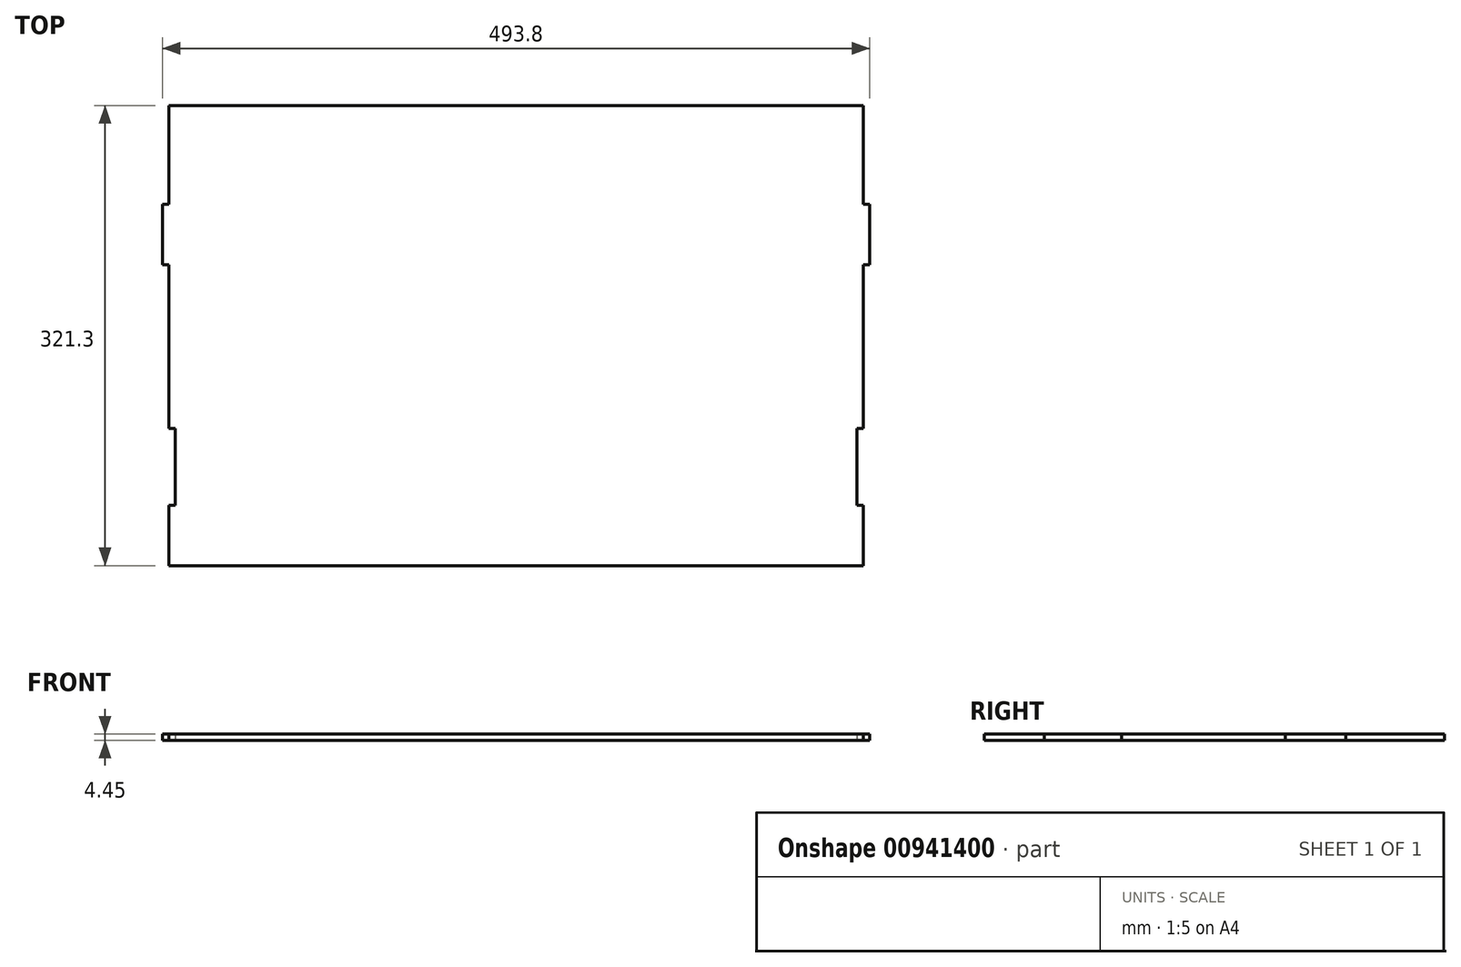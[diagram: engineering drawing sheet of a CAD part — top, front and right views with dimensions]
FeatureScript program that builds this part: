
annotation { "Feature Type Name" : "Feature", "Feature Type Description" : "" }
export const myFeature = defineFeature(function(context is Context, id is Id, definition is map)
    precondition{}
    {
        {
            var Q0;
            Q0=qCreatedBy(makeId("Top.planeOp"),FACE);
            var sketch = newSketch(context, id + "F0", { "sketchPlane" : qUnion([Q0])});
            skLineSegment(sketch, "E0.bottom", {"start": v(238, -73.7) * mm, "end": v(-238, -73.7) * mm});
            skLineSegment(sketch, "E0.left", {"start": v(238, -31.63) * mm, "end": v(238, 22.07) * mm});
            skLineSegment(sketch, "E1.bottom", {"start": v(238, 75.7) * mm, "end": v(242.45, 75.7) * mm});
            skLineSegment(sketch, "E1.top", {"start": v(238, 22.07) * mm, "end": v(242.45, 22.07) * mm});
            skLineSegment(sketch, "E1.right", {"start": v(242.45, 75.7) * mm, "end": v(242.45, 22.07) * mm});
            skLineSegment(sketch, "E2.bottom", {"start": v(238, -73.7) * mm, "end": v(242.45, -73.7) * mm});
            skLineSegment(sketch, "E2.top", {"start": v(238, -31.63) * mm, "end": v(242.45, -31.63) * mm});
            skLineSegment(sketch, "E2.right", {"start": v(242.45, -73.7) * mm, "end": v(242.45, -31.63) * mm});
            skLineSegment(sketch, "E3.left", {"start": v(238, 22.07) * mm, "end": v(238, -28.25) * mm});
            skLineSegment(sketch, "E4.MirrorCS", {"start": v(-242.45, -73.7) * mm, "end": v(-242.45, -31.63) * mm});
            skLineSegment(sketch, "E5.MirrorCS", {"start": v(-242.45, 75.7) * mm, "end": v(-242.45, 22.07) * mm});
            skLineSegment(sketch, "E6.MirrorCS", {"start": v(-238, 22.07) * mm, "end": v(-242.45, 22.07) * mm});
            skLineSegment(sketch, "E7.MirrorCS", {"start": v(-238, -31.63) * mm, "end": v(-238, 22.07) * mm});
            skLineSegment(sketch, "E8.MirrorCS", {"start": v(-238, -31.63) * mm, "end": v(-242.45, -31.63) * mm});
            skLineSegment(sketch, "E9.MirrorCS", {"start": v(-238, -73.7) * mm, "end": v(-242.45, -73.7) * mm});
            skLineSegment(sketch, "E10.MirrorCS", {"start": v(-238, 75.7) * mm, "end": v(-242.45, 75.7) * mm});
            skLineSegment(sketch, "E11.top", {"start": v(-232.45, 247.6) * mm, "end": v(232.45, 247.6) * mm});
            skLineSegment(sketch, "E11.left", {"start": v(-242.45, 75.7) * mm, "end": v(-242.45, 136.6) * mm});
            skLineSegment(sketch, "E11.right", {"start": v(242.45, 77.7) * mm, "end": v(242.45, 136.6) * mm});
            skPoint(sketch, "E12.visualSharp", {"position": v(-242.45, 247.6) * mm});
            skPoint(sketch, "E13.visualSharp", {"position": v(242.45, 247.6) * mm});
            skLineSegment(sketch, "E14.bottom", {"start": v(246.9, 136.6) * mm, "end": v(242.45, 136.6) * mm});
            skLineSegment(sketch, "E14.top", {"start": v(246.9, 178.7) * mm, "end": v(242.45, 178.7) * mm});
            skLineSegment(sketch, "E14.left", {"start": v(246.9, 136.6) * mm, "end": v(246.9, 178.7) * mm});
            skPoint(sketch, "E14.middle", {"position": v(242.45, 157.65) * mm});
            skPoint(sketch, "E14.right.start.orphan", {"position": v(238, 136.6) * mm});
            skLineSegment(sketch, "E15.trimOffspring", {"start": v(242.45, 178.7) * mm, "end": v(242.45, 237.6) * mm});
            skPoint(sketch, "E16.trimOffspring.end.orphan", {"position": v(238, 178.7) * mm});
            skLineSegment(sketch, "E17", {"start": v(-242.45, 237.6) * mm, "end": v(-242.45, 247.6) * mm});
            skLineSegment(sketch, "E18", {"start": v(-232.45, 247.6) * mm, "end": v(-242.45, 247.6) * mm});
            skLineSegment(sketch, "E19", {"start": v(232.45, 247.6) * mm, "end": v(242.45, 247.6) * mm});
            skLineSegment(sketch, "E20", {"start": v(242.45, 237.6) * mm, "end": v(242.45, 247.6) * mm});
            skLineSegment(sketch, "E21.MirrorCS", {"start": v(-246.9, 136.6) * mm, "end": v(-246.9, 178.7) * mm});
            skLineSegment(sketch, "E22.MirrorCS", {"start": v(-246.9, 136.6) * mm, "end": v(-242.45, 136.6) * mm});
            skLineSegment(sketch, "E23.MirrorCS", {"start": v(-246.9, 178.7) * mm, "end": v(-242.45, 178.7) * mm});
            skLineSegment(sketch, "E24.trimOffspring", {"start": v(-242.45, 178.7) * mm, "end": v(-242.45, 237.6) * mm});
            skLineSegment(sketch, "E25", {"start": v(242.45, 77.7) * mm, "end": v(242.45, 75.7) * mm});
            skSolve(sketch);
        }
        {
            var Q0;
            Q0=makeQuery(id+"F0.imprint","IMPRINT",FACE,{"disambiguationData":[TD([[makeQuery(id+"F0.imprint","IMPRINT",EDGE,{"derivedFrom":sQuery(id+"F0.wireOp",EDGE,"E0.bottom")}),-1.0]])]});
            var Q1;
            Q1=makeQuery(id+"F0.imprint","IMPRINT",FACE,{"disambiguationData":[TD([[makeQuery(id+"F0.imprint","IMPRINT",EDGE,{"derivedFrom":sQuery(id+"F0.wireOp",EDGE,"E11.bottom")}),1.0]])]});
            extrude(context, id + "F1", {"entities" : qUnion([Q0, Q1]), "depth" : 4.45 * mm, "offsetDistance" : 25 * mm});
        }
    });
